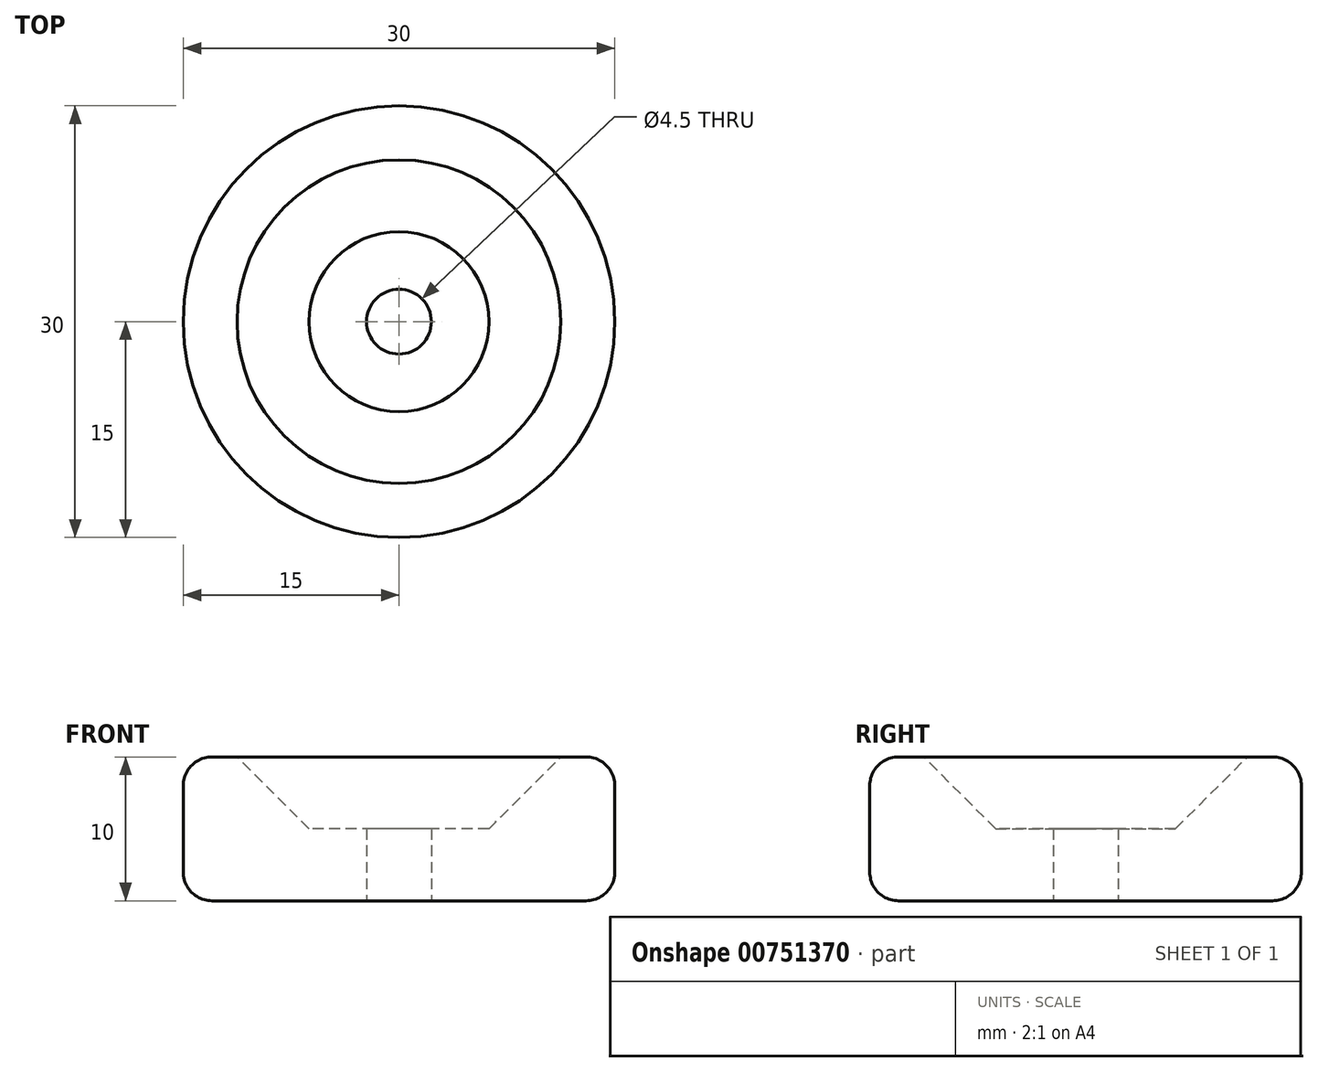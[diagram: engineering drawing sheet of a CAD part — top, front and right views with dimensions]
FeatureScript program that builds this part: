
annotation { "Feature Type Name" : "Feature", "Feature Type Description" : "" }
export const myFeature = defineFeature(function(context is Context, id is Id, definition is map)
    precondition{}
    {
        {
            var Q0;
            Q0=qCreatedBy(makeId("Top.planeOp"),FACE);
            var sketch = newSketch(context, id + "F0", { "sketchPlane" : qUnion([Q0])});
            skCircle(sketch, "E0", {"center": v(0, 0) * mm, "radius": 15 * mm});
            skCircle(sketch, "E1", {"center": v(0, 0) * mm, "radius": 2.25 * mm});
            skCircle(sketch, "E2.0", {"center": v(0, 0) * mm, "radius": 11 * mm});
            skCircle(sketch, "E3.0", {"center": v(0, 0) * mm, "radius": 4.25 * mm});
            skSolve(sketch);
        }
        {
            var Q0;
            Q0=makeQuery(id+"F0.imprint","IMPRINT",FACE,{"disambiguationData":[TD([[makeQuery(id+"F0.imprint","IMPRINT",EDGE,{"derivedFrom":sQuery(id+"F0.wireOp",EDGE,"E0")}),1.0]])]});
            var Q1;
            Q1=makeQuery(id+"F0.imprint","IMPRINT",FACE,{"disambiguationData":[TD([[makeQuery(id+"F0.imprint","IMPRINT",EDGE,{"derivedFrom":sQuery(id+"F0.wireOp",EDGE,"E2.0")}),1.0]])]});
            extrude(context, id + "F1", {"entities" : qUnion([Q0, Q1]), "depth" : 10 * mm, "offsetDistance" : 25 * mm});
        }
        {
            var Q0;
            Q0=makeQuery(id+"F1.opExtrude","CAP_EDGE",EDGE,{"disambiguationData":[OSD([sQuery(id+"F0.wireOp",EDGE,"E0")])],"isStart":false});
            var Q1;
            Q1=makeQuery(id+"F1.opExtrude","SWEPT_FACE",FACE,{"disambiguationData":[OSD([sQuery(id+"F0.wireOp",EDGE,"E0")])]});
            fillet(context, id + "F2", {"entities" : qUnion([Q0, Q1]), "radius" : 2 * mm, "tangentPropagation" : true, "allowEdgeOverflow" : false});
        }
        {
            var Q0;
            Q0=makeQuery(id+"F0.imprint","IMPRINT",FACE,{"disambiguationData":[TD([[makeQuery(id+"F0.imprint","IMPRINT",EDGE,{"derivedFrom":sQuery(id+"F0.wireOp",EDGE,"E1")}),-1.0]])]});
            extrude(context, id + "F3", {"entities" : qUnion([Q0]), "operationType" : NewBodyOperationType.ADD, "depth" : 5 * mm, "offsetDistance" : 25 * mm});
        }
        {
            var Q0;
            Q0=makeQuery(id+"F1.opExtrude","CAP_EDGE",EDGE,{"disambiguationData":[OSD([sQuery(id+"F0.wireOp",EDGE,"E3.0")])],"isStart":false});
            chamfer(context, id + "F4", {"entities" : qUnion([Q0]), "width" : 7 * mm, "tangentPropagation" : true});
        }
    });
